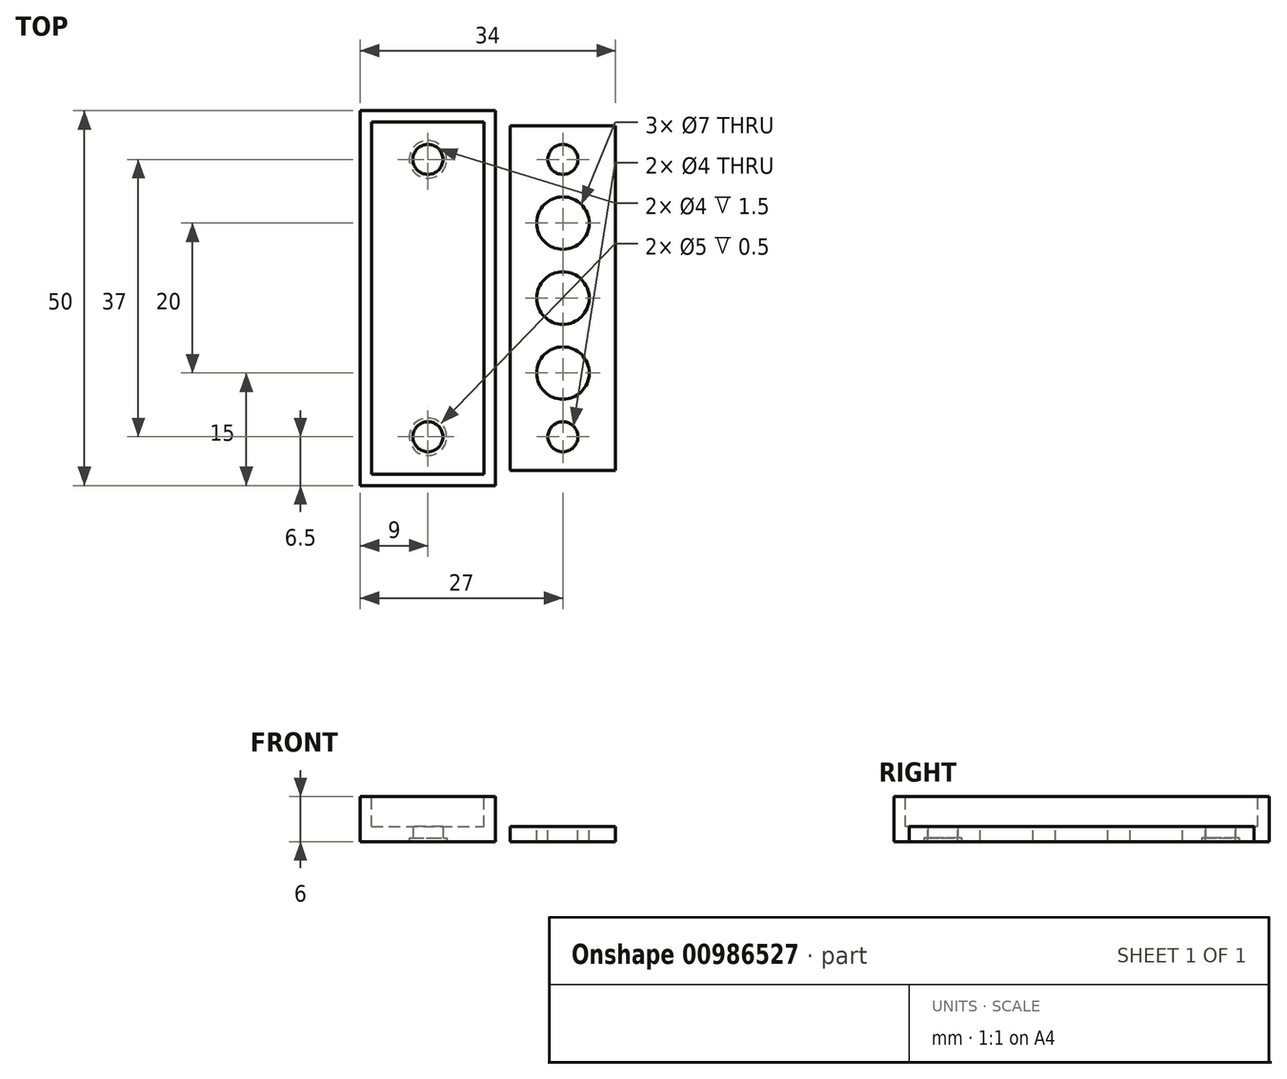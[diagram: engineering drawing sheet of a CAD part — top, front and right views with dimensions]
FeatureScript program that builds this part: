
annotation { "Feature Type Name" : "Feature", "Feature Type Description" : "" }
export const myFeature = defineFeature(function(context is Context, id is Id, definition is map)
    precondition{}
    {
        {
            var Q0;
            Q0=qCreatedBy(makeId("Top.planeOp"),FACE);
            var sketch = newSketch(context, id + "F0", { "sketchPlane" : qUnion([Q0])});
            skLineSegment(sketch, "E0.bottom", {"start": v(9, 25) * mm, "end": v(-9, 25) * mm});
            skLineSegment(sketch, "E0.top", {"start": v(9, -25) * mm, "end": v(-9, -25) * mm});
            skLineSegment(sketch, "E0.left", {"start": v(9, 25) * mm, "end": v(9, -25) * mm});
            skLineSegment(sketch, "E0.right", {"start": v(-9, 25) * mm, "end": v(-9, -25) * mm});
            skPoint(sketch, "E0.middle", {"position": v(0, 0) * mm});
            skLineSegment(sketch, "E1", {"start": v(0, 0) * mm, "end": v(0, 25) * mm});
            skLineSegment(sketch, "E2", {"start": v(0, 25) * mm, "end": v(0, 0) * mm});
            skLineSegment(sketch, "E3", {"start": v(0, -25) * mm, "end": v(0, 0) * mm});
            skSolve(sketch);
        }
        {
            var Q0;
            Q0=makeQuery(id+"F0.imprint","IMPRINT",FACE,{"disambiguationData":[TD([[makeQuery(id+"F0.imprint","IMPRINT",EDGE,{"derivedFrom":sQuery(id+"F0.wireOp",EDGE,"E0.bottom")}),1.0]])]});
            extrude(context, id + "F1", {"entities" : qUnion([Q0]), "depth" : 6 * mm, "offsetDistance" : 25 * mm});
        }
        {
            var Q0;
            Q0=makeQuery(id+"F1.opExtrude","CAP_FACE",FACE,{"disambiguationData":[OSD([sQuery(id+"F0.wireOp",EDGE,"E0.bottom"),sQuery(id+"F0.wireOp",EDGE,"E0.top"),sQuery(id+"F0.wireOp",EDGE,"E0.left"),sQuery(id+"F0.wireOp",EDGE,"E0.right")])],"isStart":false});
            var sketch = newSketch(context, id + "F2", { "sketchPlane" : qUnion([Q0])});
            skLineSegment(sketch, "E4", {"start": v(-9, 25) * mm, "end": v(-9, 23.5) * mm});
            skLineSegment(sketch, "E5", {"start": v(-9, 25) * mm, "end": v(-7.5, 25) * mm});
            skLineSegment(sketch, "E6", {"start": v(-9, 23.5) * mm, "end": v(-7.5, 23.5) * mm});
            skLineSegment(sketch, "E7", {"start": v(-7.5, 23.5) * mm, "end": v(-7.5, 25) * mm});
            skLineSegment(sketch, "E8.bottom", {"start": v(-7.5, 23.5) * mm, "end": v(7.5, 23.5) * mm});
            skLineSegment(sketch, "E8.top", {"start": v(-7.5, -23.5) * mm, "end": v(7.5, -23.5) * mm});
            skLineSegment(sketch, "E8.left", {"start": v(-7.5, 23.5) * mm, "end": v(-7.5, -23.5) * mm});
            skLineSegment(sketch, "E8.right", {"start": v(7.5, 23.5) * mm, "end": v(7.5, -23.5) * mm});
            skPoint(sketch, "E8.middle", {"position": v(0, 0) * mm});
            skSolve(sketch);
        }
        {
            var Q0;
            Q0=makeQuery(id+"F2.imprint","IMPRINT",FACE,{"disambiguationData":[TD([[makeQuery(id+"F2.imprint","IMPRINT",EDGE,{"derivedFrom":sQuery(id+"F2.wireOp",EDGE,"E8.bottom")}),-1.0]])]});
            extrude(context, id + "F3", {"entities" : qUnion([Q0]), "operationType" : NewBodyOperationType.REMOVE, "oppositeDirection" : true, "depth" : 4 * mm, "offsetDistance" : 25 * mm});
        }
        {
            var Q0;
            Q0=makeQuery(id+"F1.opExtrude","CAP_FACE",FACE,{"disambiguationData":[OSD([sQuery(id+"F0.wireOp",EDGE,"E0.bottom"),sQuery(id+"F0.wireOp",EDGE,"E0.top"),sQuery(id+"F0.wireOp",EDGE,"E0.left"),sQuery(id+"F0.wireOp",EDGE,"E0.right")])],"isStart":true});
            var sketch = newSketch(context, id + "F4", { "sketchPlane" : qUnion([Q0])});
            skLineSegment(sketch, "E9", {"start": v(0, -25) * mm, "end": v(0, -18.5) * mm});
            skLineSegment(sketch, "E10", {"start": v(0, 25) * mm, "end": v(0, 18.5) * mm});
            skLineSegment(sketch, "E11", {"start": v(0, 0) * mm, "end": v(0, -16.5) * mm});
            skLineSegment(sketch, "E12", {"start": v(0, 0) * mm, "end": v(0, 16.5) * mm});
            skSolve(sketch);
        }
        {
            var Q0;
            Q0=sQuery(id+"F4.wireOp",VERTEX,"E9.end");
            var Q1;
            Q1=sQuery(id+"F4.wireOp",VERTEX,"E10.end");
            var Q2;
            Q2=makeQuery(id+"F1.opExtrude","SWEPT_BODY",BODY,{"disambiguationData":[OSD([sQuery(id+"F0.wireOp",EDGE,"E0.bottom"),sQuery(id+"F0.wireOp",EDGE,"E0.top"),sQuery(id+"F0.wireOp",EDGE,"E0.left"),sQuery(id+"F0.wireOp",EDGE,"E0.right")])]});
            hole(context, id + "F5", {"style" : HoleStyle.C_BORE, "endStyle" : HoleEndStyle.BLIND, "holeDiameter" : 4 * mm, "cBoreDiameter" : 5 * mm, "cBoreDepth" : 0.5 * mm, "majorDiameter" : 5 * mm, "holeDepth" : 5 * mm, "isTappedThrough" : true, "tappedDepth" : 12 * mm, "tapClearance" : 3, "locations" : qUnion([Q0, Q1]), "scope" : qUnion([Q2])});
        }
        {
            var Q0;
            Q0=qCreatedBy(makeId("Top.planeOp"),FACE);
            var sketch = newSketch(context, id + "F6", { "sketchPlane" : qUnion([Q0])});
            skLineSegment(sketch, "E13", {"start": v(0, 0) * mm, "end": v(25, 0) * mm});
            skLineSegment(sketch, "E14.bottom", {"start": v(18, 23) * mm, "end": v(32, 23) * mm});
            skLineSegment(sketch, "E14.top", {"start": v(18, -23) * mm, "end": v(32, -23) * mm});
            skLineSegment(sketch, "E14.left", {"start": v(18, 23) * mm, "end": v(18, -23) * mm});
            skLineSegment(sketch, "E14.right", {"start": v(32, 23) * mm, "end": v(32, -23) * mm});
            skPoint(sketch, "E14.middle", {"position": v(25, 0) * mm});
            skSolve(sketch);
        }
        {
            var Q0;
            {var subQ0=sQuery(id+"F6.wireOp",EDGE,"E14.bottom");Q0=makeQuery(id+"F6.imprint","IMPRINT",FACE,{"disambiguationData":[TD([[makeQuery(id+"F6.imprint","IMPRINT",EDGE,{"derivedFrom":subQ0}),-1.0]])]});}
            extrude(context, id + "F7", {"entities" : qUnion([Q0]), "depth" : 2 * mm, "offsetDistance" : 25 * mm});
        }
        {
            var Q0;
            Q0=makeQuery(id+"F7.opExtrude","CAP_FACE",FACE,{"disambiguationData":[OSD([sQuery(id+"F6.wireOp",EDGE,"E14.bottom"),sQuery(id+"F6.wireOp",EDGE,"E14.top"),sQuery(id+"F6.wireOp",EDGE,"E14.left"),sQuery(id+"F6.wireOp",EDGE,"E14.right")])],"isStart":false});
            var sketch = newSketch(context, id + "F8", { "sketchPlane" : qUnion([Q0])});
            skLineSegment(sketch, "E15", {"start": v(25, -23) * mm, "end": v(25, -18.5) * mm});
            skLineSegment(sketch, "E16", {"start": v(25, 23) * mm, "end": v(25, 18.5) * mm});
            skLineSegment(sketch, "E17", {"start": v(32, 0) * mm, "end": v(18, 0) * mm});
            skLineSegment(sketch, "E18", {"start": v(25, 0) * mm, "end": v(25, 10) * mm});
            skLineSegment(sketch, "E19", {"start": v(25, 0) * mm, "end": v(25, -10) * mm});
            skPoint(sketch, "E20", {"position": v(25, -18.5) * mm});
            skPoint(sketch, "E21", {"position": v(25, -10) * mm});
            skPoint(sketch, "E22", {"position": v(25, 0) * mm});
            skPoint(sketch, "E23", {"position": v(25, 10) * mm});
            skPoint(sketch, "E24", {"position": v(25, 18.5) * mm});
            skSolve(sketch);
        }
        {
            var Q0;
            Q0=sQuery(id+"F8.wireOp",VERTEX,"E15.end");
            var Q1;
            Q1=sQuery(id+"F8.wireOp",VERTEX,"E16.end");
            var Q2;
            Q2=makeQuery(id+"F7.opExtrude","SWEPT_BODY",BODY,{"disambiguationData":[OSD([sQuery(id+"F6.wireOp",EDGE,"E14.bottom"),sQuery(id+"F6.wireOp",EDGE,"E14.top"),sQuery(id+"F6.wireOp",EDGE,"E14.left"),sQuery(id+"F6.wireOp",EDGE,"E14.right")])]});
            hole(context, id + "F9", {"style" : HoleStyle.SIMPLE, "endStyle" : HoleEndStyle.THROUGH, "holeDiameter" : 4 * mm, "majorDiameter" : 5 * mm, "isTappedThrough" : true, "tappedDepth" : 12 * mm, "tapClearance" : 3, "locations" : qUnion([Q0, Q1]), "scope" : qUnion([Q2])});
        }
        {
            var Q0;
            Q0=sQuery(id+"F8.wireOp",VERTEX,"E23");
            var Q1;
            Q1=sQuery(id+"F8.wireOp",VERTEX,"E22");
            var Q2;
            Q2=sQuery(id+"F8.wireOp",VERTEX,"E21");
            var Q3;
            Q3=makeQuery(id+"F7.opExtrude","SWEPT_BODY",BODY,{"disambiguationData":[OSD([sQuery(id+"F6.wireOp",EDGE,"E14.bottom"),sQuery(id+"F6.wireOp",EDGE,"E14.top"),sQuery(id+"F6.wireOp",EDGE,"E14.left"),sQuery(id+"F6.wireOp",EDGE,"E14.right")])]});
            hole(context, id + "F10", {"style" : HoleStyle.SIMPLE, "endStyle" : HoleEndStyle.THROUGH, "holeDiameter" : 7 * mm, "majorDiameter" : 5 * mm, "isTappedThrough" : true, "tappedDepth" : 12 * mm, "tapClearance" : 3, "startFromSketch" : true, "locations" : qUnion([Q0, Q1, Q2]), "scope" : qUnion([Q3])});
        }
        {
            var Q0;
            Q0=makeQuery(id+"F7.opExtrude","SWEPT_BODY",BODY,{"disambiguationData":[OSD([sQuery(id+"F6.wireOp",EDGE,"E14.bottom"),sQuery(id+"F6.wireOp",EDGE,"E14.top"),sQuery(id+"F6.wireOp",EDGE,"E14.left"),sQuery(id+"F6.wireOp",EDGE,"E14.right")])]});
            transform(context, id + "F11", {"entities" : qUnion([Q0]), "transformType" : TransformType.TRANSLATION_3D, "dx" : -7 * mm, "dy" : 0 * mm, "dz" : 0 * mm, "makeCopy" : false});
        }
    });
